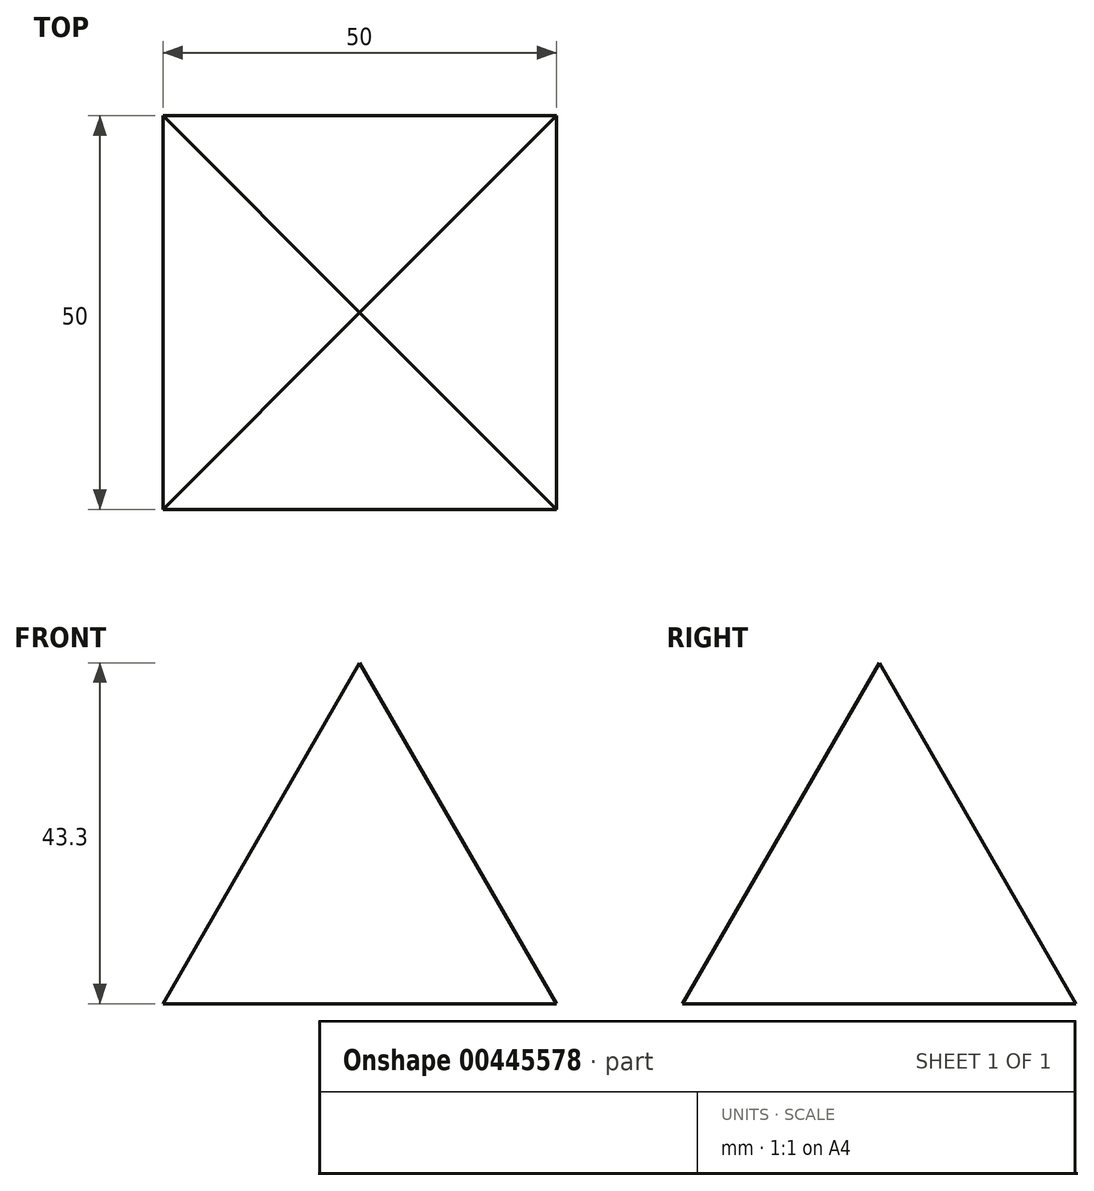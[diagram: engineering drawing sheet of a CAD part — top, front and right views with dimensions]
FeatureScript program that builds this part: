
annotation { "Feature Type Name" : "Feature", "Feature Type Description" : "" }
export const myFeature = defineFeature(function(context is Context, id is Id, definition is map)
    precondition{}
    {
        {
            var Q0;
            Q0=qCreatedBy(makeId("Top.planeOp"),FACE);
            var sketch = newSketch(context, id + "F0", { "sketchPlane" : qUnion([Q0])});
            skLineSegment(sketch, "E0.bottom", {"start": v(25, -25) * mm, "end": v(-25, -25) * mm});
            skLineSegment(sketch, "E0.top", {"start": v(25, 25) * mm, "end": v(-25, 25) * mm});
            skLineSegment(sketch, "E0.left", {"start": v(25, -25) * mm, "end": v(25, 25) * mm});
            skLineSegment(sketch, "E0.right", {"start": v(-25, -25) * mm, "end": v(-25, 25) * mm});
            skPoint(sketch, "E0.middle", {"position": v(0, 0) * mm});
            skSolve(sketch);
        }
        {
            var Q0;
            Q0 = qSketchRegion(id + "F0", true);
            extrude(context, id + "F1", {"entities" : qUnion([Q0]), "depth" : 50 * mm, "hasDraft" : true, "draftAngle" : 30 * degree, "draftPullDirection" : true});
        }
    });
